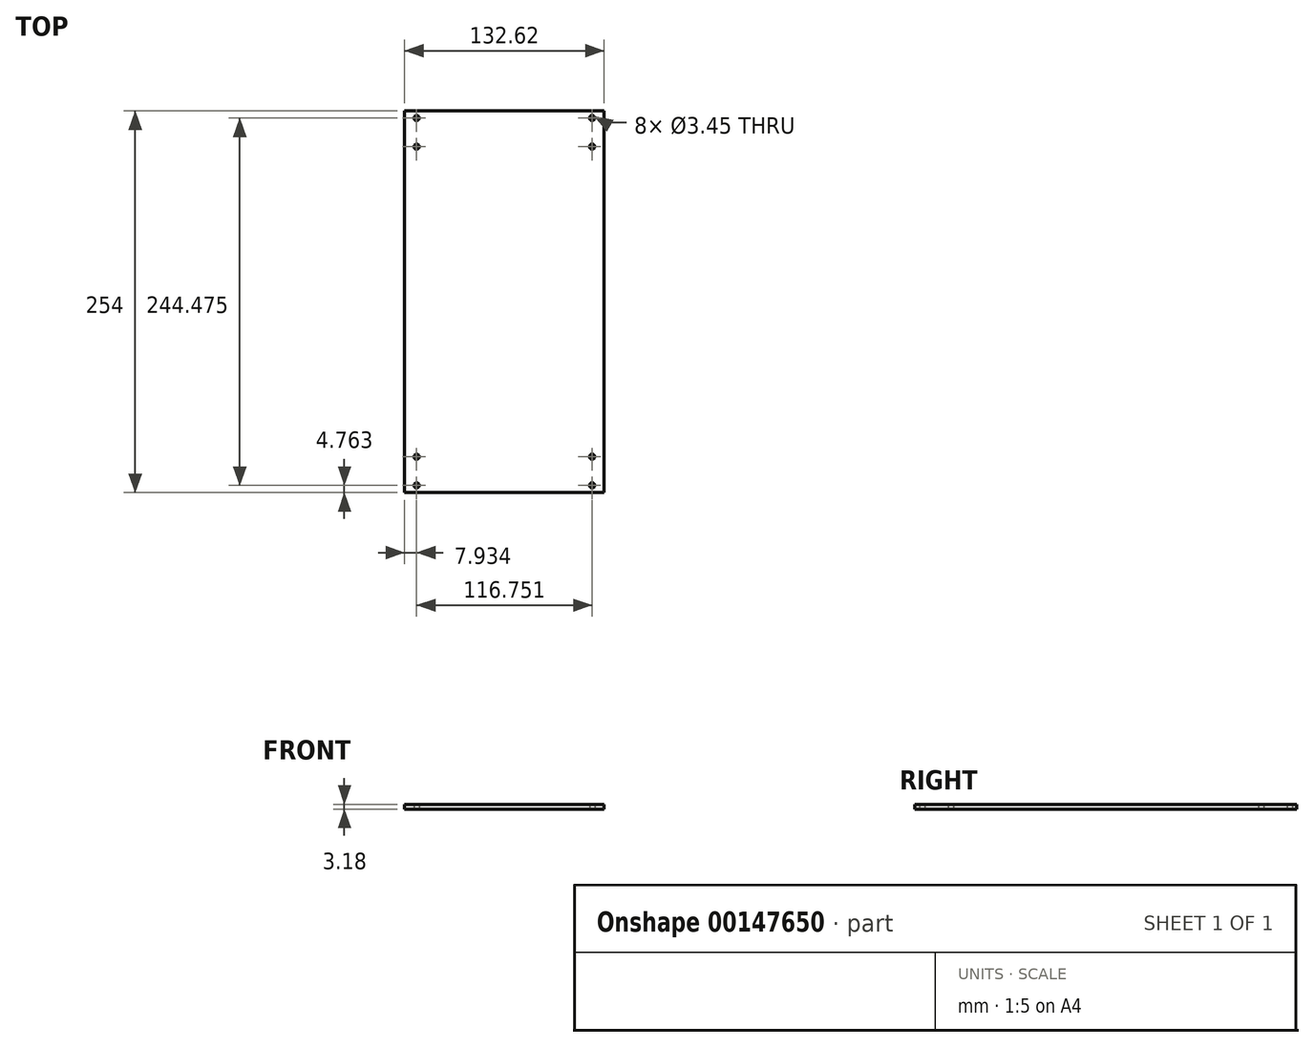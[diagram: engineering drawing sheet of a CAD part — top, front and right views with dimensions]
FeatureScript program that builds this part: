
annotation { "Feature Type Name" : "Feature", "Feature Type Description" : "" }
export const myFeature = defineFeature(function(context is Context, id is Id, definition is map)
    precondition{}
    {
        {
            var Q0;
            Q0=qCreatedBy(makeId("Top.planeOp"),FACE);
            var sketch = newSketch(context, id + "F0", { "sketchPlane" : qUnion([Q0])});
            skLineSegment(sketch, "E0.bottom", {"start": v(66.31, -127) * mm, "end": v(-66.31, -127) * mm});
            skLineSegment(sketch, "E0.top", {"start": v(66.31, 127) * mm, "end": v(-66.31, 127) * mm});
            skLineSegment(sketch, "E0.left", {"start": v(66.31, -127) * mm, "end": v(66.31, 127) * mm});
            skLineSegment(sketch, "E0.right", {"start": v(-66.31, -127) * mm, "end": v(-66.31, 127) * mm});
            skPoint(sketch, "E0.middle", {"position": v(0, 0) * mm});
            skLineSegment(sketch, "E1", {"start": v(58.38, 103.19) * mm, "end": v(66.31, 103.19) * mm, "construction": true});
            skLineSegment(sketch, "E2.bottom", {"start": v(58.38, 103.19) * mm, "end": v(-58.38, 103.19) * mm, "construction": true});
            skLineSegment(sketch, "E2.top", {"start": v(58.38, -103.19) * mm, "end": v(-58.38, -103.19) * mm, "construction": true});
            skLineSegment(sketch, "E2.left", {"start": v(58.38, 103.19) * mm, "end": v(58.38, -103.19) * mm, "construction": true});
            skLineSegment(sketch, "E2.right", {"start": v(-58.38, 103.19) * mm, "end": v(-58.38, -103.19) * mm, "construction": true});
            skCircle(sketch, "E3", {"center": v(58.38, 103.19) * mm, "radius": 1.73 * mm});
            skCircle(sketch, "E4", {"center": v(-58.38, -103.19) * mm, "radius": 1.73 * mm});
            skLineSegment(sketch, "E5", {"start": v(0, 103.19) * mm, "end": v(0, 127) * mm, "construction": true});
            skLineSegment(sketch, "E6", {"start": v(58.38, 103.19) * mm, "end": v(58.38, 122.24) * mm, "construction": true});
            skCircle(sketch, "E7", {"center": v(-58.38, 103.19) * mm, "radius": 1.73 * mm});
            skCircle(sketch, "E8", {"center": v(58.38, -103.19) * mm, "radius": 1.73 * mm});
            skLineSegment(sketch, "E9", {"start": v(58.38, 122.24) * mm, "end": v(58.38, 127) * mm, "construction": true});
            skCircle(sketch, "E10", {"center": v(58.38, 122.24) * mm, "radius": 1.73 * mm});
            skLineSegment(sketch, "E11", {"start": v(-58.38, 103.19) * mm, "end": v(-58.38, 122.24) * mm, "construction": true});
            skLineSegment(sketch, "E12", {"start": v(-58.38, 122.24) * mm, "end": v(-58.38, 127) * mm, "construction": true});
            skLineSegment(sketch, "E13", {"start": v(-58.38, -103.19) * mm, "end": v(-58.38, -122.24) * mm, "construction": true});
            skLineSegment(sketch, "E14", {"start": v(-58.38, -122.24) * mm, "end": v(-58.38, -127) * mm, "construction": true});
            skLineSegment(sketch, "E15", {"start": v(58.38, -103.19) * mm, "end": v(58.38, -122.24) * mm, "construction": true});
            skLineSegment(sketch, "E16", {"start": v(58.38, -122.24) * mm, "end": v(58.38, -127) * mm, "construction": true});
            skCircle(sketch, "E17", {"center": v(-58.38, 122.24) * mm, "radius": 1.73 * mm});
            skCircle(sketch, "E18", {"center": v(-58.38, -122.24) * mm, "radius": 1.73 * mm});
            skCircle(sketch, "E19", {"center": v(58.38, -122.24) * mm, "radius": 1.73 * mm});
            skSolve(sketch);
        }
        {
            var Q0;
            Q0=makeQuery(id+"F0.imprint","IMPRINT",FACE,{"disambiguationData":[TD([[makeQuery(id+"F0.imprint","IMPRINT",EDGE,{"derivedFrom":sQuery(id+"F0.wireOp",EDGE,"E0.bottom")}),-1.0]])]});
            extrude(context, id + "F1", {"entities" : qUnion([Q0]), "depth" : 3.17 * mm});
        }
    });
